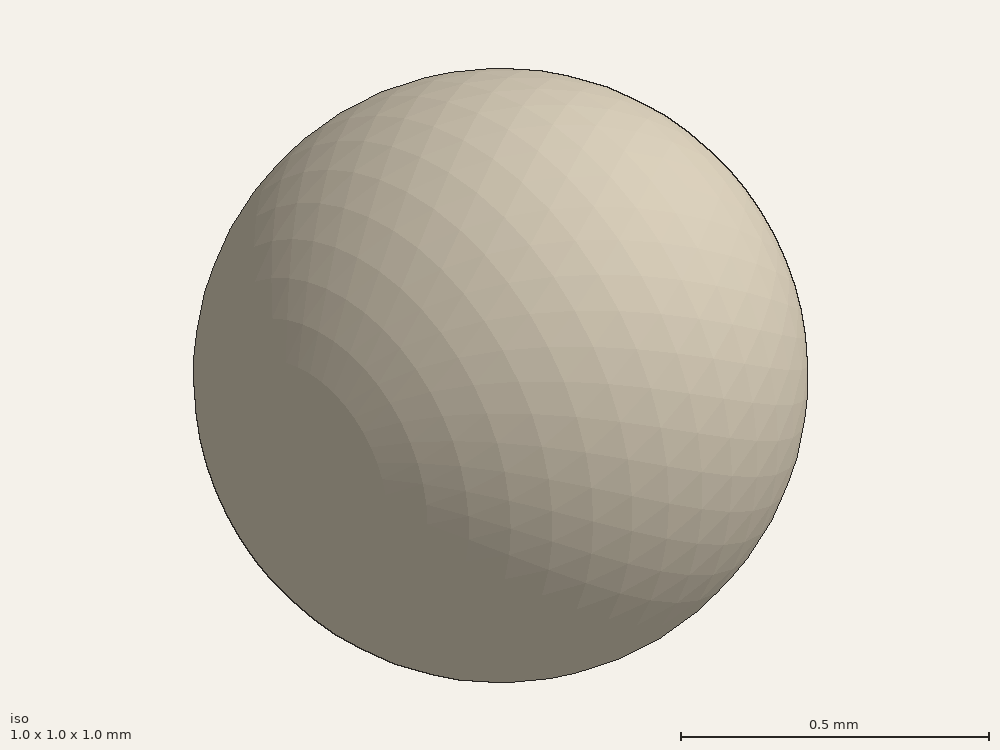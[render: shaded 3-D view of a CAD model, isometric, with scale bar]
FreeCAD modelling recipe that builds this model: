
FCSTD DOCUMENT  (FreeCAD 1.2R45145 (Git))
Label: JointBall
License: All rights reserved
LicenseURL: https://en.wikipedia.org/wiki/All_rights_reserved
objects: App::Point×1, Sketcher::SketchObject×1, PartDesign::Revolution×1, PartDesign::Body×1
note: 6 computed .brp shape members not serialized (recipe doc carries the construction recipe); baked Part::Feature solids carry a one-line shape summary decoded from their .brp

FEATURE [App::Point] Origin001
  Role = Origin
FEATURE [Sketcher::SketchObject] Sketch
  ArcFitTolerance = 1e-06
  AttachmentSupport = -> [Origin]
  ExternalTypes = [0]
  FullyConstrained = true
  MakeInternals = false
  MapMode = 5
  sketch-geometry (2):
    g0: ArcOfCircle CenterX=0 CenterY=0 CenterZ=0 NormalX=0 NormalY=0 NormalZ=1 AngleXU=0 Radius=0.5 StartAngle=0 EndAngle=3.14159
    g1: LineSegment StartX=-0.5 StartY=0 StartZ=0 EndX=0.5 EndY=0 EndZ=0
  constraints (6):
    c: Coincident(g1,g0)
    c: Coincident(g1,g0)
    c: Horizontal(g1)
    c: Radius(g0) = 0.5
    c: PointOnObject(g0,g-1)
    c: Coincident(g0,g-1)
FEATURE [PartDesign::Revolution] Revolution
  Angle = 360
  Angle2 = 60
  Axis = (1,0,0)
  Base = (0,0,0)
  FuseOrder = 0
  Profile = -> Sketch
  ReferenceAxis = -> Sketch [H_Axis]
  Refine = true
  Suppressed = false
  Type = 0
FEATURE [PartDesign::Body] Body  label="Ball"
  AllowCompound = false
  Group = -> [Sketch,Revolution]
  Origin = -> Origin
  Tip = -> Revolution
